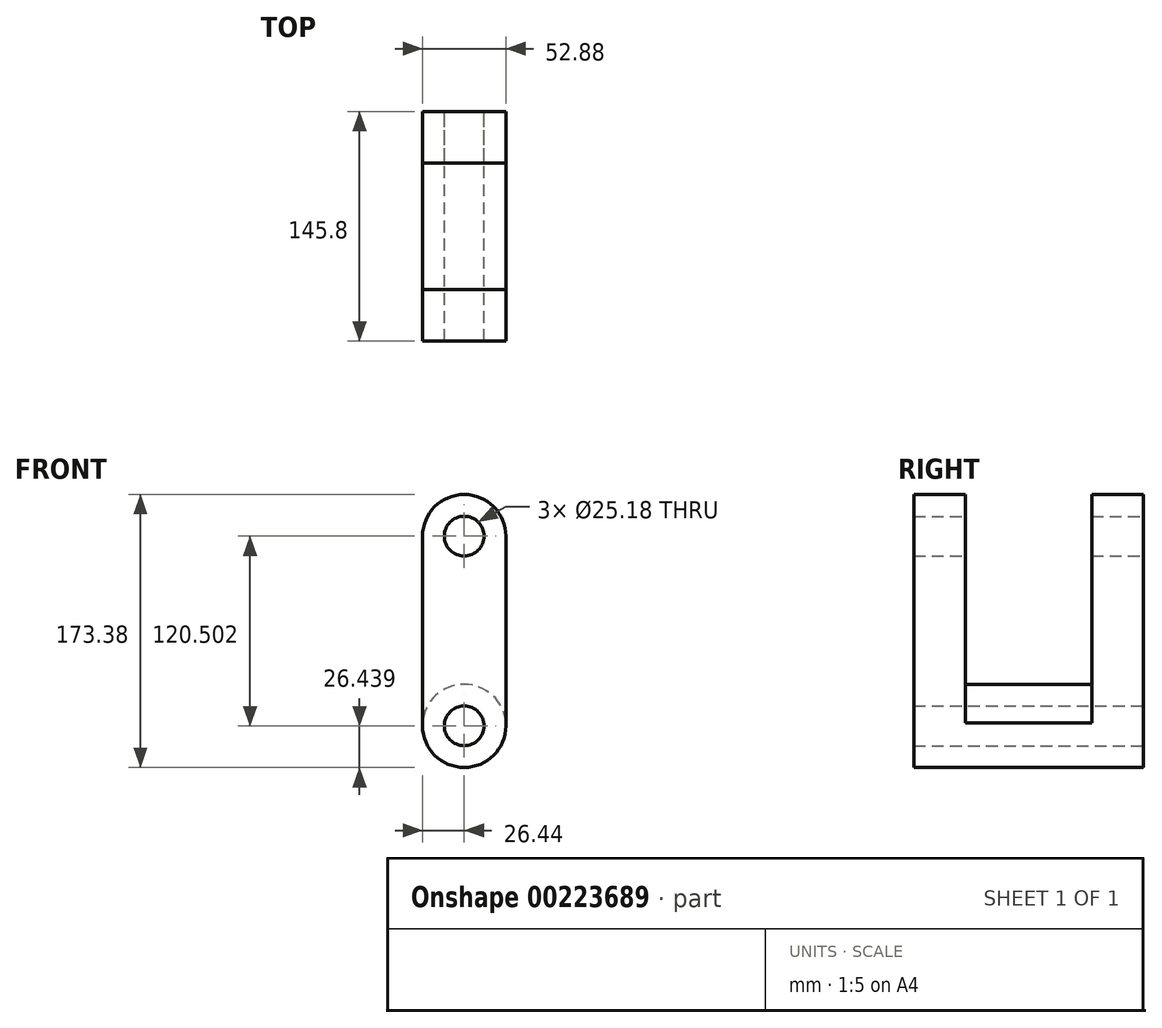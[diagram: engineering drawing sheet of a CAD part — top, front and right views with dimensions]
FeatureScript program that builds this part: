
annotation { "Feature Type Name" : "Feature", "Feature Type Description" : "" }
export const myFeature = defineFeature(function(context is Context, id is Id, definition is map)
    precondition{}
    {
        {
            var Q0;
            Q0=qCreatedBy(makeId("Front.planeOp"),FACE);
            var sketch = newSketch(context, id + "F0", { "sketchPlane" : qUnion([Q0])});
            skLineSegment(sketch, "E0.left", {"start": v(26.44, 60.25) * mm, "end": v(26.44, -60.25) * mm});
            skLineSegment(sketch, "E0.right", {"start": v(-26.44, 60.25) * mm, "end": v(-26.44, -60.25) * mm});
            skPoint(sketch, "E0.middle", {"position": v(0, 0) * mm});
            skArc(sketch, "E1", {"start": v(26.44, 60.25) * mm, "mid": v(0, 86.69) * mm, "end": v(-26.44, 60.25) * mm});
            skArc(sketch, "E2", {"start": v(-26.44, -60.25) * mm, "mid": v(0, -86.69) * mm, "end": v(26.44, -60.25) * mm});
            skCircle(sketch, "E3", {"center": v(0, 60.25) * mm, "radius": 12.6 * mm});
            skCircle(sketch, "E4.MirrorC", {"center": v(0, -60.25) * mm, "radius": 12.6 * mm});
            skSolve(sketch);
        }
        {
            var Q0;
            Q0=makeQuery(id+"F0.imprint","IMPRINT",FACE,{"disambiguationData":[TD([[makeQuery(id+"F0.imprint","IMPRINT",EDGE,{"derivedFrom":sQuery(id+"F0.wireOp",EDGE,"E0.left")}),-1.0]])]});
            extrude(context, id + "F1", {"entities" : qUnion([Q0]), "endBound" : BoundingType.SYMMETRIC, "depth" : 145.8 * mm});
        }
        {
            var Q0;
            Q0=qCreatedBy(makeId("Front.planeOp"),FACE);
            var sketch = newSketch(context, id + "F2", { "sketchPlane" : qUnion([Q0])});
            skLineSegment(sketch, "E5.bottom", {"start": v(26.5, 60.32) * mm, "end": v(-26.5, 60.32) * mm});
            skLineSegment(sketch, "E5.left", {"start": v(26.5, 60.32) * mm, "end": v(26.5, -60.32) * mm});
            skLineSegment(sketch, "E5.right", {"start": v(-26.5, 60.32) * mm, "end": v(-26.5, -60.32) * mm});
            skPoint(sketch, "E5.middle", {"position": v(0, 0) * mm});
            skCircle(sketch, "E6", {"center": v(0, 60.32) * mm, "radius": 26.5 * mm});
            skArc(sketch, "E7", {"start": v(26.5, -60.32) * mm, "mid": v(0, -33.81) * mm, "end": v(-26.5, -60.32) * mm});
            skSolve(sketch);
        }
        {
            var Q0;
            Q0 = qSketchRegion(id + "F2", true);
            extrude(context, id + "F3", {"entities" : qUnion([Q0]), "operationType" : NewBodyOperationType.REMOVE, "endBound" : BoundingType.SYMMETRIC, "oppositeDirection" : true, "depth" : 80.26 * mm});
        }
    });
